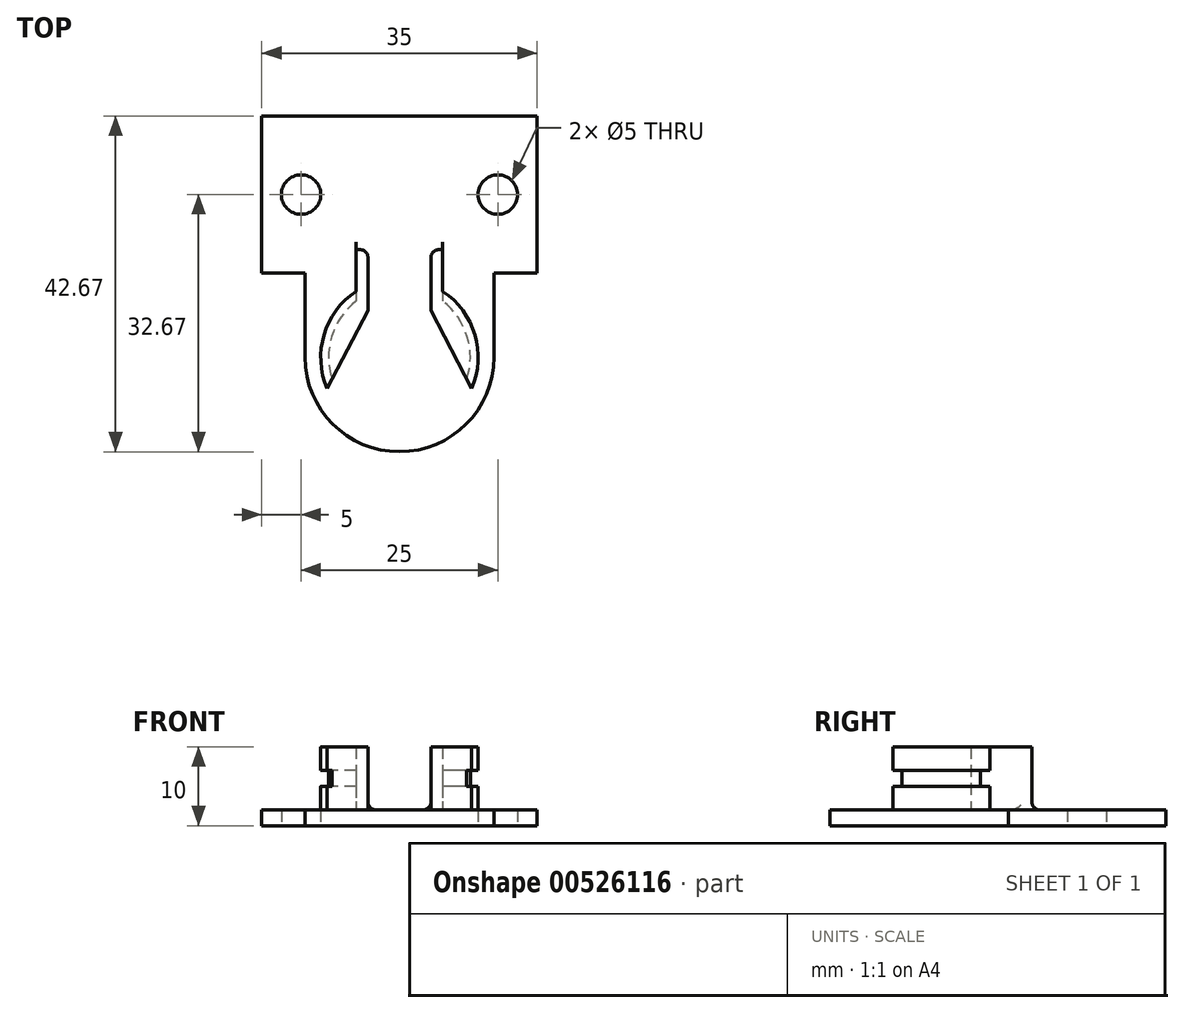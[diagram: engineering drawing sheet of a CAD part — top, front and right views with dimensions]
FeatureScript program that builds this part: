
annotation { "Feature Type Name" : "Feature", "Feature Type Description" : "" }
export const myFeature = defineFeature(function(context is Context, id is Id, definition is map)
    precondition{}
    {
        {
            var Q0;
            Q0=qCreatedBy(makeId("Top.planeOp"),FACE);
            var sketch = newSketch(context, id + "F0", { "sketchPlane" : qUnion([Q0])});
            skArc(sketch, "E0", {"start": v(-5.5, 1.5) * mm, "mid": v(0, 24.17) * mm, "end": v(5.5, 1.5) * mm});
            skArc(sketch, "E1", {"start": v(-5.5, -1.5) * mm, "mid": v(0, -24.17) * mm, "end": v(5.5, -1.5) * mm});
            skLineSegment(sketch, "E2", {"start": v(-5.5, 1.5) * mm, "end": v(-5.5, -1.5) * mm});
            skLineSegment(sketch, "E3", {"start": v(5.5, 1.5) * mm, "end": v(5.5, -1.5) * mm});
            skSolve(sketch);
        }
        {
            var Q0;
            Q0=qSketchRegion(id+"F0",true);
            extrude(context, id + "F1", {"entities" : qUnion([Q0]), "depth" : 2 * mm, "offsetDistance" : 25 * mm});
        }
        {
            var Q0;
            Q0=makeQuery(id+"F1.opExtrude","CAP_FACE",FACE,{"disambiguationData":[OSD([sQuery(id+"F0.wireOp",EDGE,"E0"),sQuery(id+"F0.wireOp",EDGE,"E1"),sQuery(id+"F0.wireOp",EDGE,"E2"),sQuery(id+"F0.wireOp",EDGE,"E3")])],"isStart":false});
            var sketch = newSketch(context, id + "F2", { "sketchPlane" : qUnion([Q0])});
            skArc(sketch, "E4", {"start": v(8.66, 17.17) * mm, "mid": v(9.5, 9.04) * mm, "end": v(4, 3) * mm});
            skArc(sketch, "E5", {"start": v(9.78, 19.11) * mm, "mid": v(11.66, 9.33) * mm, "end": v(5.5, 1.5) * mm});
            skArc(sketch, "E6", {"start": v(-8.66, 17.17) * mm, "mid": v(-9.5, 9.04) * mm, "end": v(-4, 3) * mm});
            skArc(sketch, "E7", {"start": v(5.5, -3.81) * mm, "mid": v(9.59, -9.32) * mm, "end": v(9.17, -16.17) * mm});
            skLineSegment(sketch, "E8", {"start": v(9.78, 19.11) * mm, "end": v(8.66, 17.17) * mm});
            skLineSegment(sketch, "E9", {"start": v(-8.66, 17.17) * mm, "end": v(-9.78, 19.11) * mm});
            skLineSegment(sketch, "E10", {"start": v(5.5, 1.5) * mm, "end": v(5.5, -3.81) * mm});
            skLineSegment(sketch, "E11", {"start": v(-4, 3) * mm, "end": v(-4, -6.24) * mm});
            skLineSegment(sketch, "E12", {"start": v(-4, -6.24) * mm, "end": v(-9.17, -16.17) * mm});
            skLineSegment(sketch, "E13", {"start": v(9.17, -16.17) * mm, "end": v(4, -6.24) * mm});
            skLineSegment(sketch, "E14", {"start": v(4, -6.24) * mm, "end": v(4, 3) * mm});
            skArc(sketch, "E15", {"start": v(-9.78, 19.11) * mm, "mid": v(-11.66, 9.33) * mm, "end": v(-5.5, 1.5) * mm});
            skArc(sketch, "E16", {"start": v(-9.17, -16.17) * mm, "mid": v(-9.59, -9.32) * mm, "end": v(-5.5, -3.81) * mm});
            skLineSegment(sketch, "E17", {"start": v(-5.5, 1.5) * mm, "end": v(-5.5, -3.81) * mm});
            skArc(sketch, "E18.0", {"start": v(-5.5, 1.5) * mm, "mid": v(0, 24.17) * mm, "end": v(5.5, 1.5) * mm, "construction": true});
            skArc(sketch, "E19.0", {"start": v(-5.5, -1.5) * mm, "mid": v(0, -24.17) * mm, "end": v(5.5, -1.5) * mm, "construction": true});
            skSolve(sketch);
        }
        {
            var Q0;
            Q0=qSketchRegion(id+"F2",true);
            extrude(context, id + "F3", {"entities" : qUnion([Q0]), "operationType" : NewBodyOperationType.ADD, "depth" : 3 * mm, "offsetDistance" : 25 * mm});
        }
        {
            var Q0;
            Q0=makeQuery(id+"F3.opExtrude","CAP_FACE",FACE,{"disambiguationData":[OSD([sQuery(id+"F2.wireOp",EDGE,"E4"),sQuery(id+"F2.wireOp",EDGE,"E5"),sQuery(id+"F2.wireOp",EDGE,"E7"),sQuery(id+"F2.wireOp",EDGE,"E8"),sQuery(id+"F2.wireOp",EDGE,"E10"),sQuery(id+"F2.wireOp",EDGE,"E13"),sQuery(id+"F2.wireOp",EDGE,"E14")])],"isStart":false});
            var sketch = newSketch(context, id + "F4", { "sketchPlane" : qUnion([Q0])});
            skArc(sketch, "E20", {"start": v(-9.78, 19.11) * mm, "mid": v(-11.66, 9.33) * mm, "end": v(-5.5, 1.5) * mm});
            skArc(sketch, "E21", {"start": v(9.78, 19.11) * mm, "mid": v(11.66, 9.33) * mm, "end": v(5.5, 1.5) * mm});
            skArc(sketch, "E22", {"start": v(8.07, 16.15) * mm, "mid": v(8.53, 9.28) * mm, "end": v(4, 4.1) * mm});
            skArc(sketch, "E23", {"start": v(-8.07, 16.15) * mm, "mid": v(-8.53, 9.28) * mm, "end": v(-4, 4.1) * mm});
            skArc(sketch, "E24", {"start": v(5.5, -5.04) * mm, "mid": v(8.6, -9.53) * mm, "end": v(8.55, -14.98) * mm});
            skArc(sketch, "E25", {"start": v(-5.5, -5.04) * mm, "mid": v(-8.6, -9.53) * mm, "end": v(-8.55, -14.98) * mm});
            skLineSegment(sketch, "E26", {"start": v(-5.5, 1.5) * mm, "end": v(-5.5, -5.04) * mm});
            skLineSegment(sketch, "E27", {"start": v(5.5, 1.5) * mm, "end": v(5.5, -5.04) * mm});
            skLineSegment(sketch, "E28", {"start": v(-4, 4.1) * mm, "end": v(-4, -6.24) * mm});
            skLineSegment(sketch, "E29", {"start": v(-4, -6.24) * mm, "end": v(-8.55, -14.98) * mm});
            skLineSegment(sketch, "E30", {"start": v(4, 4.1) * mm, "end": v(4, -6.24) * mm});
            skLineSegment(sketch, "E31", {"start": v(4, -6.24) * mm, "end": v(8.55, -14.98) * mm});
            skLineSegment(sketch, "E32", {"start": v(8.07, 16.15) * mm, "end": v(9.78, 19.11) * mm});
            skLineSegment(sketch, "E33", {"start": v(-9.78, 19.11) * mm, "end": v(-8.07, 16.15) * mm});
            skLineSegment(sketch, "E34.0", {"start": v(-8.66, 17.17) * mm, "end": v(-9.78, 19.11) * mm, "construction": true});
            skLineSegment(sketch, "E35.0", {"start": v(9.78, 19.11) * mm, "end": v(8.66, 17.17) * mm, "construction": true});
            skLineSegment(sketch, "E36.0", {"start": v(-4, -6.24) * mm, "end": v(-9.17, -16.17) * mm, "construction": true});
            skLineSegment(sketch, "E37.0", {"start": v(9.17, -16.17) * mm, "end": v(4, -6.24) * mm, "construction": true});
            skArc(sketch, "E38.0", {"start": v(-9.78, 19.11) * mm, "mid": v(0, 24.17) * mm, "end": v(9.78, 19.11) * mm, "construction": true});
            skArc(sketch, "E39.0", {"start": v(-5.5, -1.5) * mm, "mid": v(0, -24.17) * mm, "end": v(5.5, -1.5) * mm, "construction": true});
            skSolve(sketch);
        }
        {
            var Q0;
            Q0=qSketchRegion(id+"F4",true);
            extrude(context, id + "F5", {"entities" : qUnion([Q0]), "operationType" : NewBodyOperationType.ADD, "depth" : 2 * mm, "offsetDistance" : 25 * mm});
        }
        {
            var Q0;
            Q0=makeQuery(id+"F5.opExtrude","CAP_FACE",FACE,{"disambiguationData":[OSD([sQuery(id+"F4.wireOp",EDGE,"E21"),sQuery(id+"F4.wireOp",EDGE,"E22"),sQuery(id+"F4.wireOp",EDGE,"E24"),sQuery(id+"F4.wireOp",EDGE,"E27"),sQuery(id+"F4.wireOp",EDGE,"E30"),sQuery(id+"F4.wireOp",EDGE,"E31"),sQuery(id+"F4.wireOp",EDGE,"E32")])],"isStart":false});
            var sketch = newSketch(context, id + "F6", { "sketchPlane" : qUnion([Q0])});
            skArc(sketch, "E40", {"start": v(8.66, 17.17) * mm, "mid": v(9.5, 9.04) * mm, "end": v(4, 3) * mm});
            skArc(sketch, "E41", {"start": v(9.78, 19.11) * mm, "mid": v(11.66, 9.33) * mm, "end": v(5.5, 1.5) * mm});
            skArc(sketch, "E42", {"start": v(-8.66, 17.17) * mm, "mid": v(-9.5, 9.04) * mm, "end": v(-4, 3) * mm});
            skArc(sketch, "E43", {"start": v(5.5, -3.81) * mm, "mid": v(9.59, -9.32) * mm, "end": v(9.17, -16.17) * mm});
            skLineSegment(sketch, "E44", {"start": v(9.78, 19.11) * mm, "end": v(8.66, 17.17) * mm});
            skLineSegment(sketch, "E45", {"start": v(-8.66, 17.17) * mm, "end": v(-9.78, 19.11) * mm});
            skLineSegment(sketch, "E46", {"start": v(5.5, 1.5) * mm, "end": v(5.5, -3.81) * mm});
            skLineSegment(sketch, "E47", {"start": v(-4, 3) * mm, "end": v(-4, -6.24) * mm});
            skLineSegment(sketch, "E48", {"start": v(-4, -6.24) * mm, "end": v(-9.17, -16.17) * mm});
            skLineSegment(sketch, "E49", {"start": v(9.17, -16.17) * mm, "end": v(4, -6.24) * mm});
            skLineSegment(sketch, "E50", {"start": v(4, -6.24) * mm, "end": v(4, 3) * mm});
            skArc(sketch, "E51", {"start": v(-9.78, 19.11) * mm, "mid": v(-11.66, 9.33) * mm, "end": v(-5.5, 1.5) * mm});
            skArc(sketch, "E52", {"start": v(-9.17, -16.17) * mm, "mid": v(-9.59, -9.32) * mm, "end": v(-5.5, -3.81) * mm});
            skLineSegment(sketch, "E53", {"start": v(-5.5, 1.5) * mm, "end": v(-5.5, -3.81) * mm});
            skArc(sketch, "E54.0", {"start": v(-5.5, -1.5) * mm, "mid": v(0, -24.17) * mm, "end": v(5.5, -1.5) * mm, "construction": true});
            skArc(sketch, "E55.0", {"start": v(-9.78, 19.11) * mm, "mid": v(0, 24.17) * mm, "end": v(9.78, 19.11) * mm, "construction": true});
            skSolve(sketch);
        }
        {
            var Q0;
            Q0=qSketchRegion(id+"F6",true);
            extrude(context, id + "F7", {"entities" : qUnion([Q0]), "operationType" : NewBodyOperationType.ADD, "depth" : 3 * mm, "offsetDistance" : 25 * mm});
        }
        {
            var Q0;
            Q0=makeQuery(id+"F5.opExtrude","CAP_EDGE",EDGE,{"disambiguationData":[OSD([sQuery(id+"F4.wireOp",EDGE,"E22")])],"isStart":false});
            var Q1;
            Q1=makeQuery(id+"F5.opExtrude","CAP_EDGE",EDGE,{"disambiguationData":[OSD([sQuery(id+"F4.wireOp",EDGE,"E23")])],"isStart":false});
            var Q2;
            Q2=makeQuery(id+"F5.opExtrude","CAP_EDGE",EDGE,{"disambiguationData":[OSD([sQuery(id+"F4.wireOp",EDGE,"E23")])],"isStart":true});
            var Q3;
            Q3=makeQuery(id+"F5.opExtrude","CAP_EDGE",EDGE,{"disambiguationData":[OSD([sQuery(id+"F4.wireOp",EDGE,"E22")])],"isStart":true});
            var Q4;
            Q4=makeQuery(id+"F5.opExtrude","CAP_EDGE",EDGE,{"disambiguationData":[OSD([sQuery(id+"F4.wireOp",EDGE,"E25")])],"isStart":true});
            var Q5;
            Q5=makeQuery(id+"F5.opExtrude","CAP_EDGE",EDGE,{"disambiguationData":[OSD([sQuery(id+"F4.wireOp",EDGE,"E25")])],"isStart":false});
            var Q6;
            Q6=makeQuery(id+"F5.opExtrude","CAP_EDGE",EDGE,{"disambiguationData":[OSD([sQuery(id+"F4.wireOp",EDGE,"E24")])],"isStart":false});
            var Q7;
            Q7=makeQuery(id+"F5.opExtrude","CAP_EDGE",EDGE,{"disambiguationData":[OSD([sQuery(id+"F4.wireOp",EDGE,"E24")])],"isStart":true});
            fillet(context, id + "F8", {"entities" : qUnion([Q0, Q1, Q2, Q3, Q4, Q5, Q6, Q7]), "radius" : 1 * mm, "tangentPropagation" : true, "allowEdgeOverflow" : false});
        }
        {
            var Q0;
            Q0=makeQuery(id+"F7.opExtrude","CAP_FACE",FACE,{"disambiguationData":[OSD([sQuery(id+"F6.wireOp",EDGE,"E40"),sQuery(id+"F6.wireOp",EDGE,"E41"),sQuery(id+"F6.wireOp",EDGE,"E43"),sQuery(id+"F6.wireOp",EDGE,"E44"),sQuery(id+"F6.wireOp",EDGE,"E46"),sQuery(id+"F6.wireOp",EDGE,"E49"),sQuery(id+"F6.wireOp",EDGE,"E50")])],"isStart":false});
            var sketch = newSketch(context, id + "F9", { "sketchPlane" : qUnion([Q0])});
            skLineSegment(sketch, "E56.bottom", {"start": v(-12, 1.5) * mm, "end": v(12, 1.5) * mm});
            skLineSegment(sketch, "E56.top", {"start": v(-12, 24.17) * mm, "end": v(12, 24.17) * mm});
            skLineSegment(sketch, "E56.left", {"start": v(-12, 24.17) * mm, "end": v(-12, 1.5) * mm});
            skLineSegment(sketch, "E56.right", {"start": v(12, 24.17) * mm, "end": v(12, 1.5) * mm});
            skSolve(sketch);
        }
        {
            var Q0;
            Q0=qSketchRegion(id+"F9",true);
            extrude(context, id + "F10", {"entities" : qUnion([Q0]), "operationType" : NewBodyOperationType.REMOVE, "oppositeDirection" : true, "depth" : 10 * mm, "offsetDistance" : 25 * mm});
        }
        {
            var Q0;
            Q0=makeQuery(id+"F1.opExtrude","CAP_FACE",FACE,{"disambiguationData":[OSD([sQuery(id+"F0.wireOp",EDGE,"E0"),sQuery(id+"F0.wireOp",EDGE,"E1"),sQuery(id+"F0.wireOp",EDGE,"E2"),sQuery(id+"F0.wireOp",EDGE,"E3")])],"isStart":true});
            var sketch = newSketch(context, id + "F11", { "sketchPlane" : qUnion([Q0])});
            skLineSegment(sketch, "E57", {"start": v(12, 12.17) * mm, "end": v(-12, 12.17) * mm});
            skLineSegment(sketch, "E58", {"start": v(-12, 1.5) * mm, "end": v(-12, 12.17) * mm});
            skLineSegment(sketch, "E59", {"start": v(-12, 1.5) * mm, "end": v(-17.5, 1.5) * mm});
            skLineSegment(sketch, "E60", {"start": v(-17.5, -18.5) * mm, "end": v(-17.5, 1.5) * mm});
            skLineSegment(sketch, "E61", {"start": v(-17.5, -18.5) * mm, "end": v(17.5, -18.5) * mm});
            skLineSegment(sketch, "E62", {"start": v(17.5, 1.5) * mm, "end": v(17.5, -18.5) * mm});
            skLineSegment(sketch, "E63", {"start": v(17.5, 1.5) * mm, "end": v(12, 1.5) * mm});
            skLineSegment(sketch, "E64", {"start": v(12, 12.17) * mm, "end": v(12, 1.5) * mm});
            skCircle(sketch, "E65", {"center": v(-12.5, -8.5) * mm, "radius": 2.5 * mm});
            skCircle(sketch, "E66", {"center": v(12.5, -8.5) * mm, "radius": 2.5 * mm});
            skSolve(sketch);
        }
        {
            var Q0;
            Q0=qSketchRegion(id+"F11",true);
            extrude(context, id + "F12", {"entities" : qUnion([Q0]), "operationType" : NewBodyOperationType.ADD, "oppositeDirection" : true, "depth" : 2 * mm, "offsetDistance" : 25 * mm});
        }
        {
            var Q0;
            Q0=makeQuery(id+"F10.boolean.opBoolean","INTERSECT",EDGE,{"derivedFrom":[makeQuery(id+"F7.boolean.opBoolean","MERGE",FACE,{"derivedFrom":[makeQuery(id+"F5.boolean.opBoolean","MERGE",FACE,{"derivedFrom":[makeQuery(id+"F3.opExtrude","SWEPT_FACE",FACE,{"disambiguationData":[OSD([sQuery(id+"F2.wireOp",EDGE,"E11")])]}),makeQuery(id+"F5.opExtrude","SWEPT_FACE",FACE,{"disambiguationData":[OSD([sQuery(id+"F4.wireOp",EDGE,"E28")])]})]}),makeQuery(id+"F7.opExtrude","SWEPT_FACE",FACE,{"disambiguationData":[OSD([sQuery(id+"F6.wireOp",EDGE,"E47")])]})]}),makeQuery(id+"F10.opExtrude","SWEPT_FACE",FACE,{"disambiguationData":[OSD([sQuery(id+"F9.wireOp",EDGE,"E56.bottom")])]})]});
            var Q1;
            Q1=makeQuery(id+"F10.boolean.opBoolean","INTERSECT",EDGE,{"derivedFrom":[makeQuery(id+"F7.boolean.opBoolean","MERGE",FACE,{"derivedFrom":[makeQuery(id+"F5.boolean.opBoolean","MERGE",FACE,{"derivedFrom":[makeQuery(id+"F3.opExtrude","SWEPT_FACE",FACE,{"disambiguationData":[OSD([sQuery(id+"F2.wireOp",EDGE,"E14")])]}),makeQuery(id+"F5.opExtrude","SWEPT_FACE",FACE,{"disambiguationData":[OSD([sQuery(id+"F4.wireOp",EDGE,"E30")])]})]}),makeQuery(id+"F7.opExtrude","SWEPT_FACE",FACE,{"disambiguationData":[OSD([sQuery(id+"F6.wireOp",EDGE,"E50")])]})]}),makeQuery(id+"F10.opExtrude","SWEPT_FACE",FACE,{"disambiguationData":[OSD([sQuery(id+"F9.wireOp",EDGE,"E56.bottom")])]})]});
            var Q2;
            Q2=makeQuery(id+"F12.boolean.opBoolean","INTERSECT",EDGE,{"disambiguationData":[OD(0.0)],"derivedFrom":[makeQuery(id+"F10.boolean.opBoolean","COPY",FACE,{"derivedFrom":makeQuery(id+"F10.opExtrude","SWEPT_FACE",FACE,{"disambiguationData":[OSD([sQuery(id+"F9.wireOp",EDGE,"E56.bottom")])]})}),makeQuery(id+"F12.opExtrude","CAP_FACE",FACE,{"disambiguationData":[OSD([sQuery(id+"F11.wireOp",EDGE,"E57"),sQuery(id+"F11.wireOp",EDGE,"E58"),sQuery(id+"F11.wireOp",EDGE,"E59"),sQuery(id+"F11.wireOp",EDGE,"E60"),sQuery(id+"F11.wireOp",EDGE,"E61"),sQuery(id+"F11.wireOp",EDGE,"E62"),sQuery(id+"F11.wireOp",EDGE,"E63"),sQuery(id+"F11.wireOp",EDGE,"E64"),sQuery(id+"F11.wireOp",EDGE,"E65"),sQuery(id+"F11.wireOp",EDGE,"E66")])],"isStart":false})]});
            var Q3;
            Q3=makeQuery(id+"F12.boolean.opBoolean","INTERSECT",EDGE,{"disambiguationData":[OD(1.0)],"derivedFrom":[makeQuery(id+"F10.boolean.opBoolean","COPY",FACE,{"derivedFrom":makeQuery(id+"F10.opExtrude","SWEPT_FACE",FACE,{"disambiguationData":[OSD([sQuery(id+"F9.wireOp",EDGE,"E56.bottom")])]})}),makeQuery(id+"F12.opExtrude","CAP_FACE",FACE,{"disambiguationData":[OSD([sQuery(id+"F11.wireOp",EDGE,"E57"),sQuery(id+"F11.wireOp",EDGE,"E58"),sQuery(id+"F11.wireOp",EDGE,"E59"),sQuery(id+"F11.wireOp",EDGE,"E60"),sQuery(id+"F11.wireOp",EDGE,"E61"),sQuery(id+"F11.wireOp",EDGE,"E62"),sQuery(id+"F11.wireOp",EDGE,"E63"),sQuery(id+"F11.wireOp",EDGE,"E64"),sQuery(id+"F11.wireOp",EDGE,"E65"),sQuery(id+"F11.wireOp",EDGE,"E66")])],"isStart":false})]});
            var Q4;
            Q4=makeQuery(id+"F3.opExtrude","CAP_EDGE",EDGE,{"disambiguationData":[OSD([sQuery(id+"F2.wireOp",EDGE,"E13")])],"isStart":true});
            var Q5;
            Q5=makeQuery(id+"F3.opExtrude","CAP_EDGE",EDGE,{"disambiguationData":[OSD([sQuery(id+"F2.wireOp",EDGE,"E12")])],"isStart":true});
            fillet(context, id + "F13", {"entities" : qUnion([Q0, Q1, Q2, Q3, Q4, Q5]), "radius" : 1 * mm, "tangentPropagation" : true, "allowEdgeOverflow" : false});
        }
    });
